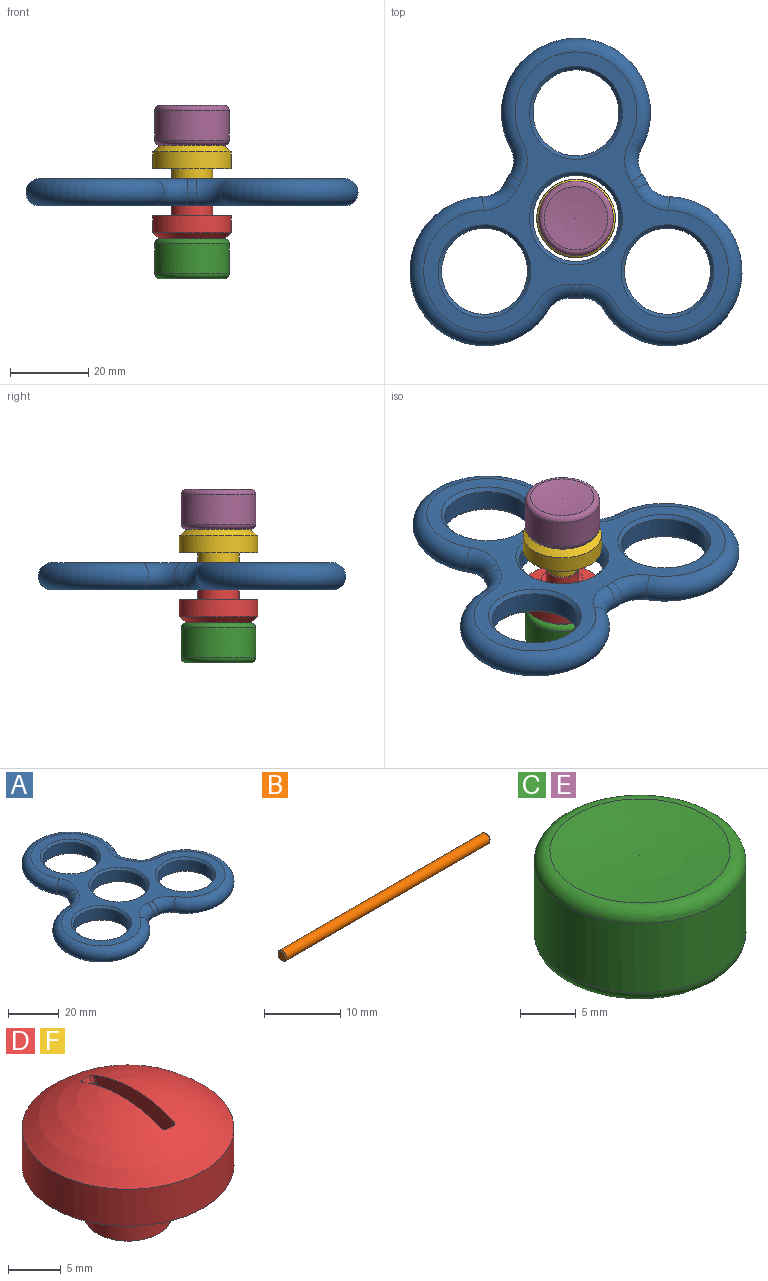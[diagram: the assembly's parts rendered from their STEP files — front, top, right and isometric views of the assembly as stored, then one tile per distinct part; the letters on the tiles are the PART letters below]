
ASSEMBLY  parts=6 mates=9
PART A: 26 faces, bbox 88x81.7x7 mm
  f0: cylinder r=10.99mm len=21.97mm, axis (0,0,-1), area 359.4mm2, adj f18,f24
  f1: cylinder r=10.99mm len=21.97mm, axis (0,0,-1), area 359.4mm2, adj f21,f22
  f2: cylinder r=10.99mm len=21.97mm, axis (0,0,-1), area 359.4mm2, adj f19,f23
  f3: cylinder r=10.99mm len=21.97mm, axis (0,0,-1), area 359.4mm2, adj f20,f25
  f4: plane 77.86x71.6mm, normal (0,0,1), area 1273.6mm2, adj f6,f7,f8,f9,f10,f11,f12,f13
  f5: plane 77.86x71.6mm, normal (0,0,-1), area 1273.6mm2, adj f6,f7,f8,f9,f10,f11,f12,f13
  f6: torus R=15.56mm, axis (0,0,1), area 808.4mm2, adj f4,f5,f7,f8
  f7: torus R=9.84mm, axis (0,0,1), area 90.9mm2, adj f4,f5,f6,f9
  f8: torus R=9.84mm, axis (0,0,1), area 90.9mm2, adj f4,f5,f6,f10
  f9: torus R=16.89mm, axis (0,0,1), area 26.2mm2, adj f4,f5,f7,f11
  f10: torus R=16.89mm, axis (0,0,1), area 26.2mm2, adj f4,f5,f8,f12
  f11: torus R=9.84mm, axis (0,0,1), area 90.9mm2, adj f4,f5,f9,f13
  f12: torus R=9.84mm, axis (0,0,1), area 90.9mm2, adj f4,f5,f10,f14
  f13: torus R=15.56mm, axis (0,0,1), area 808.4mm2, adj f4,f5,f11,f15
  f14: torus R=15.56mm, axis (0,0,1), area 808.4mm2, adj f4,f5,f12,f16
  f15: torus R=9.84mm, axis (0,0,1), area 90.9mm2, adj f4,f5,f13,f17
  f16: torus R=9.84mm, axis (0,0,1), area 90.9mm2, adj f4,f5,f14,f17
  f17: torus R=16.89mm, axis (0,0,1), area 26.2mm2, adj f4,f5,f15,f16
  f18: cone r=11.87mm half-angle=45deg, axis (0,0,-1), area 90.3mm2, adj f0,f5
  f19: cone r=11.87mm half-angle=45deg, axis (0,0,-1), area 90.3mm2, adj f2,f5
  f20: cone r=11.87mm half-angle=45deg, axis (0,0,-1), area 90.3mm2, adj f3,f5
  f21: cone r=11.87mm half-angle=45deg, axis (0,0,-1), area 90.3mm2, adj f1,f5
  f22: cone r=10.99mm half-angle=45deg, axis (0,0,1), area 90.3mm2, adj f1,f4
  f23: cone r=10.99mm half-angle=45deg, axis (0,0,1), area 90.3mm2, adj f2,f4
  f24: cone r=10.99mm half-angle=45deg, axis (0,0,1), area 90.3mm2, adj f0,f4
  f25: cone r=10.99mm half-angle=45deg, axis (0,0,1), area 90.3mm2, adj f3,f4
PART B: 5 faces, bbox 38.1x1.6x1.6 mm
  f0: plane 1.27x1.27mm, normal (1,0,0), area 1.3mm2, adj f1
  f1: cone r=0mm half-angle=45deg, axis (-1,0,0), area 1mm2, adj f0,f2
  f2: cylinder r=0.79mm len=37.78mm, axis (1,0,0), area 188.4mm2, adj f1,f4
  f3: plane 1.27x1.27mm, normal (-1,0,0), area 1.3mm2, adj f4
  f4: cone r=0mm half-angle=45deg, axis (1,0,0), area 1mm2, adj f2,f3
PART C: 7 faces, bbox 20.6x20.6x10.1 mm
  f0: cylinder r=0.83mm len=4.72mm, axis (0,0,-1), area 24.5mm2, adj f1,f4
  f1: sphere r=14.29mm, area 193.3mm2, adj f0,f5
  f2: cylinder r=9.53mm len=19.05mm, axis (0,0,-1), area 454.8mm2, adj f5,f6
  f3: sphere r=63.5mm, area 206.6mm2, adj f6
  f4: plane 1.65x1.65mm, normal (0,0,-1), area 2.1mm2, adj f0
  f5: torus R=8.26mm, axis (0,0,-1), area 148.9mm2, adj f1,f2
  f6: torus R=8.26mm, axis (0,0,1), area 121.9mm2, adj f2,f3
PART D: 29 faces, bbox 20.1x20.1x15.2 mm
  f0: plane 6.34x0.13mm, normal (0,0,-1), area 0.8mm2, adj f1,f2,f16,f18
  f1: cylinder r=3.37mm len=10.49mm, axis (0,0,-1), area 15.1mm2, adj f0,f3,f4,f13,f14,f15,f16,f17
  f2: cylinder r=3.37mm len=10.49mm, axis (0,0,-1), area 15.1mm2, adj f0,f3,f4,f13,f14,f15,f16,f17
  f3: plane 6.34x0.13mm, normal (0,0,-1), area 0.8mm2, adj f1,f2,f15,f17
  f4: plane 8.26x8.26mm, normal (0,0,-1), area 36.8mm2, adj f1,f2,f5,f15,f16
  f5: cylinder r=4.13mm len=8.26mm, axis (0,0,-1), area 87.3mm2, adj f4,f6
  f6: plane 10.54x10.54mm, normal (0,0,-1), area 33.7mm2, adj f5,f7
  f7: cylinder r=5.27mm len=10.54mm, axis (0,0,-1), area 84.1mm2, adj f6,f8
  f8: plane 20.07x20.07mm, normal (0,0,-1), area 229mm2, adj f7,f9
  f9: cylinder r=10.03mm len=20.07mm, axis (0,0,-1), area 269mm2, adj f8,f10
  f10: sphere r=14.29mm, area 350.6mm2, adj f9,f11,f12,f13,f14,f21,f23,f25
  f11: bspline ~6.73x2.98mm, area 0.7mm2, adj f10,f20,f21,f23
  f12: bspline ~6.73x2.98mm, area 0.7mm2, adj f10,f19,f25,f27
  f13: plane 10.63x7.83mm, normal (1,0,0), area 37mm2, adj f1,f2,f10,f17,f21,f22,f27,f28
  f14: plane 10.63x7.83mm, normal (-1,0,0), area 37mm2, adj f1,f2,f10,f18,f23,f24,f25,f26
  f15: plane 10.17x6.23mm, normal (1,0,0), area 63.4mm2, adj f1,f2,f3,f4
  f16: plane 10.17x6.23mm, normal (-1,0,0), area 63.4mm2, adj f0,f1,f2,f4
  f17: cylinder r=0.32mm len=6.53mm, axis (0,-1,0), area 3.2mm2, adj f1,f2,f3,f13
  f18: cylinder r=0.32mm len=6.53mm, axis (0,-1,0), area 3.2mm2, adj f0,f1,f2,f14
  f19: bspline ~9.96x2.06mm, area 9.4mm2, adj f2,f12,f26,f28
  f20: bspline ~9.96x2.06mm, area 9.4mm2, adj f1,f11,f22,f24
  f21: bspline ~2.46x1.33mm, area 0.4mm2, adj f10,f11,f13,f22
  f22: bspline ~13.94x3.69mm, area 4.6mm2, adj f1,f13,f20,f21
  f23: bspline ~2.46x1.33mm, area 0.4mm2, adj f10,f11,f14,f24
  f24: bspline ~13.35x3.68mm, area 4.6mm2, adj f1,f14,f20,f23
  f25: bspline ~2.46x1.33mm, area 0.4mm2, adj f10,f12,f14,f26
  f26: bspline ~13.93x3.69mm, area 4.6mm2, adj f2,f14,f19,f25
  f27: bspline ~2.46x1.33mm, area 0.4mm2, adj f10,f12,f13,f28
  f28: bspline ~13.35x3.68mm, area 4.6mm2, adj f2,f13,f19,f27
PART E: same geometry as C
PART F: same geometry as D
PLACE A at identity fixed
PLACE B rot(axis=(0.23,0.94,-0.23),93.3deg) t=(0,0,3.56)mm
PLACE C rot(axis=(-0.42,-0.91,0),180deg) t=(0,0,3.5)mm
PLACE D rot(axis=(0.84,0.55,0),180deg) t=(0,0,3.37)mm
PLACE E rot(axis=(0,0,1),127.9deg) t=(0,0,3.62)mm
PLACE F rot(axis=(0,0,1),158.5deg) t=(0,0,3.62)mm
MATE cylindrical F.f1 <-> A.f3  axis (0,0,-1) through (0,0,5.3)mm
MATE cylindrical B.f1 <-> E.f0  axis (0,0,-1) through (0,0,22.45)mm
MATE cylindrical A.f3 <-> D.f1  axis (0,0,-1) through (0,0,3.49)mm
MATE planar A.f3 <-> F.f1  axis (0,0,1) through (0,0,6.99)mm
MATE planar B.f1 <-> C.f0  axis (0,0,-1) through (0,0,-15.49)mm
MATE planar E.f0 <-> B.f1  axis (0,0,-1) through (0,0,22.61)mm
MATE cylindrical B.f1 <-> C.f0  axis (0,0,-1) through (0,0,22.45)mm
MATE planar A.f3 <-> D.f1  axis (0,0,-1) through (0,0,0)mm
MATE cylindrical B.f1 <-> A.f3  axis (0,0,-1) through (0,0,3.56)mm
